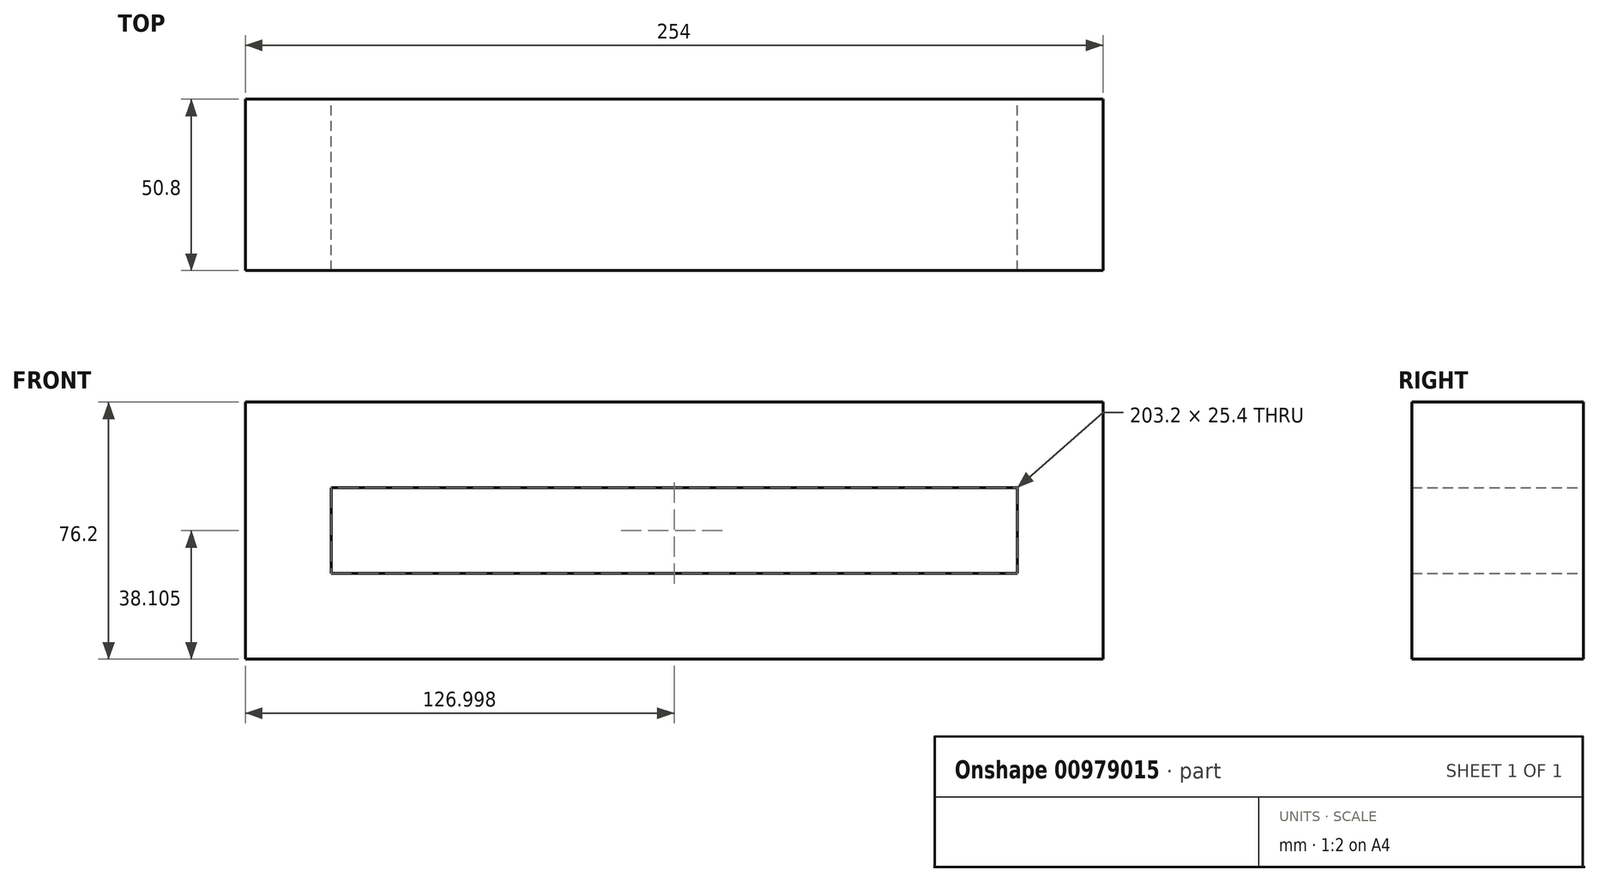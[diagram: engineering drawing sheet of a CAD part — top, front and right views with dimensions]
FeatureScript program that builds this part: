
annotation { "Feature Type Name" : "Feature", "Feature Type Description" : "" }
export const myFeature = defineFeature(function(context is Context, id is Id, definition is map)
    precondition{}
    {
        {
            var Q0;
            Q0=qCreatedBy(makeId("Front.planeOp"),FACE);
            var sketch = newSketch(context, id + "F0", { "sketchPlane" : qUnion([Q0])});
            skLineSegment(sketch, "E0.bottom", {"start": v(-117.02, 25.26) * mm, "end": v(136.98, 25.26) * mm});
            skLineSegment(sketch, "E0.top", {"start": v(-117.02, -50.94) * mm, "end": v(136.98, -50.94) * mm});
            skLineSegment(sketch, "E0.left", {"start": v(-117.02, 25.26) * mm, "end": v(-117.02, -50.94) * mm});
            skLineSegment(sketch, "E0.right", {"start": v(136.98, 25.26) * mm, "end": v(136.98, -50.94) * mm});
            skLineSegment(sketch, "E1.0", {"start": v(-91.62, -0.14) * mm, "end": v(111.58, -0.14) * mm});
            skLineSegment(sketch, "E1.1", {"start": v(-91.62, -0.14) * mm, "end": v(-91.62, -25.54) * mm});
            skLineSegment(sketch, "E1.2", {"start": v(-91.62, -25.54) * mm, "end": v(111.58, -25.54) * mm});
            skLineSegment(sketch, "E1.3", {"start": v(111.58, -0.14) * mm, "end": v(111.58, -25.54) * mm});
            skSolve(sketch);
        }
        {
            var Q0;
            Q0=makeQuery(id+"F0.imprint","IMPRINT",FACE,{"disambiguationData":[TD([[makeQuery(id+"F0.imprint","IMPRINT",EDGE,{"derivedFrom":sQuery(id+"F0.wireOp",EDGE,"E0.bottom")}),-1.0]])]});
            extrude(context, id + "F1", {"entities" : qUnion([Q0]), "depth" : 50.8 * mm, "offsetDistance" : 25.4 * mm});
        }
    });
